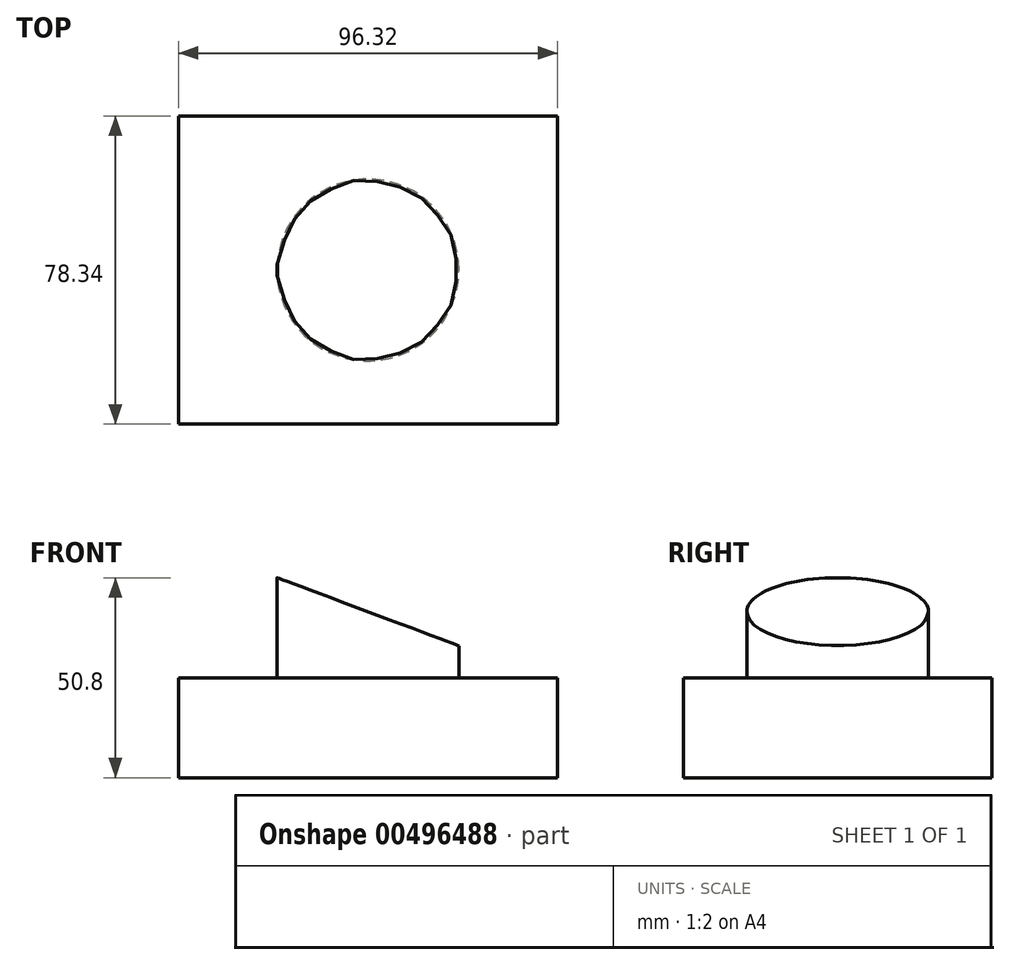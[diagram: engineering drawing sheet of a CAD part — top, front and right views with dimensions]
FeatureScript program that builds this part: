
annotation { "Feature Type Name" : "Feature", "Feature Type Description" : "" }
export const myFeature = defineFeature(function(context is Context, id is Id, definition is map)
    precondition{}
    {
        {
            var Q0;
            Q0=qCreatedBy(makeId("Top.planeOp"),FACE);
            var sketch = newSketch(context, id + "F0", { "sketchPlane" : qUnion([Q0])});
            skLineSegment(sketch, "E0.bottom", {"start": v(48.16, -39.17) * mm, "end": v(-48.16, -39.17) * mm});
            skLineSegment(sketch, "E0.top", {"start": v(48.16, 39.17) * mm, "end": v(-48.16, 39.17) * mm});
            skLineSegment(sketch, "E0.left", {"start": v(48.16, -39.17) * mm, "end": v(48.16, 39.17) * mm});
            skLineSegment(sketch, "E0.right", {"start": v(-48.16, -39.17) * mm, "end": v(-48.16, 39.17) * mm});
            skPoint(sketch, "E0.middle", {"position": v(0, 0) * mm});
            skSolve(sketch);
        }
        {
            var Q0;
            Q0=makeQuery(id+"F0.imprint","IMPRINT",FACE,{"disambiguationData":[TD([[makeQuery(id+"F0.imprint","IMPRINT",EDGE,{"derivedFrom":sQuery(id+"F0.wireOp",EDGE,"E0.bottom")}),-1.0]])]});
            extrude(context, id + "F1", {"entities" : qUnion([Q0]), "oppositeDirection" : true, "depth" : 25.4 * mm});
        }
        {
            var Q0;
            Q0=makeQuery(id+"F1.opExtrude","CAP_FACE",FACE,{"disambiguationData":[OSD([sQuery(id+"F0.wireOp",EDGE,"E0.bottom"),sQuery(id+"F0.wireOp",EDGE,"E0.top"),sQuery(id+"F0.wireOp",EDGE,"E0.left"),sQuery(id+"F0.wireOp",EDGE,"E0.right")])],"isStart":true});
            var sketch = newSketch(context, id + "F2", { "sketchPlane" : qUnion([Q0])});
            skCircle(sketch, "E1", {"center": v(0, 0) * mm, "radius": 23.1 * mm});
            skSolve(sketch);
        }
        {
            var Q0;
            Q0=makeQuery(id+"F2.imprint","IMPRINT",FACE,{"disambiguationData":[TD([[makeQuery(id+"F2.imprint","IMPRINT",EDGE,{"derivedFrom":sQuery(id+"F2.wireOp",EDGE,"E1")}),1.0]])]});
            extrude(context, id + "F3", {"entities" : qUnion([Q0]), "operationType" : NewBodyOperationType.ADD, "depth" : 25.4 * mm});
        }
        {
            var Q0;
            Q0=qCreatedBy(makeId("Front.planeOp"),FACE);
            var sketch = newSketch(context, id + "F4", { "sketchPlane" : qUnion([Q0])});
            skLineSegment(sketch, "E2", {"start": v(-23.16, 25.45) * mm, "end": v(23.16, 8.08) * mm});
            skLineSegment(sketch, "E3", {"start": v(23.16, 25.45) * mm, "end": v(-23.16, 25.45) * mm});
            skLineSegment(sketch, "E4", {"start": v(23.16, 8.08) * mm, "end": v(23.16, 25.45) * mm});
            skSolve(sketch);
        }
        {
            var Q0;
            Q0=makeQuery(id+"F4.imprint","IMPRINT",FACE,{"disambiguationData":[TD([[makeQuery(id+"F4.imprint","IMPRINT",EDGE,{"derivedFrom":sQuery(id+"F4.wireOp",EDGE,"E2")}),1.0]])]});
            extrude(context, id + "F5", {"entities" : qUnion([Q0]), "operationType" : NewBodyOperationType.REMOVE, "endBound" : BoundingType.SYMMETRIC, "oppositeDirection" : true, "depth" : 50.8 * mm});
        }
    });
